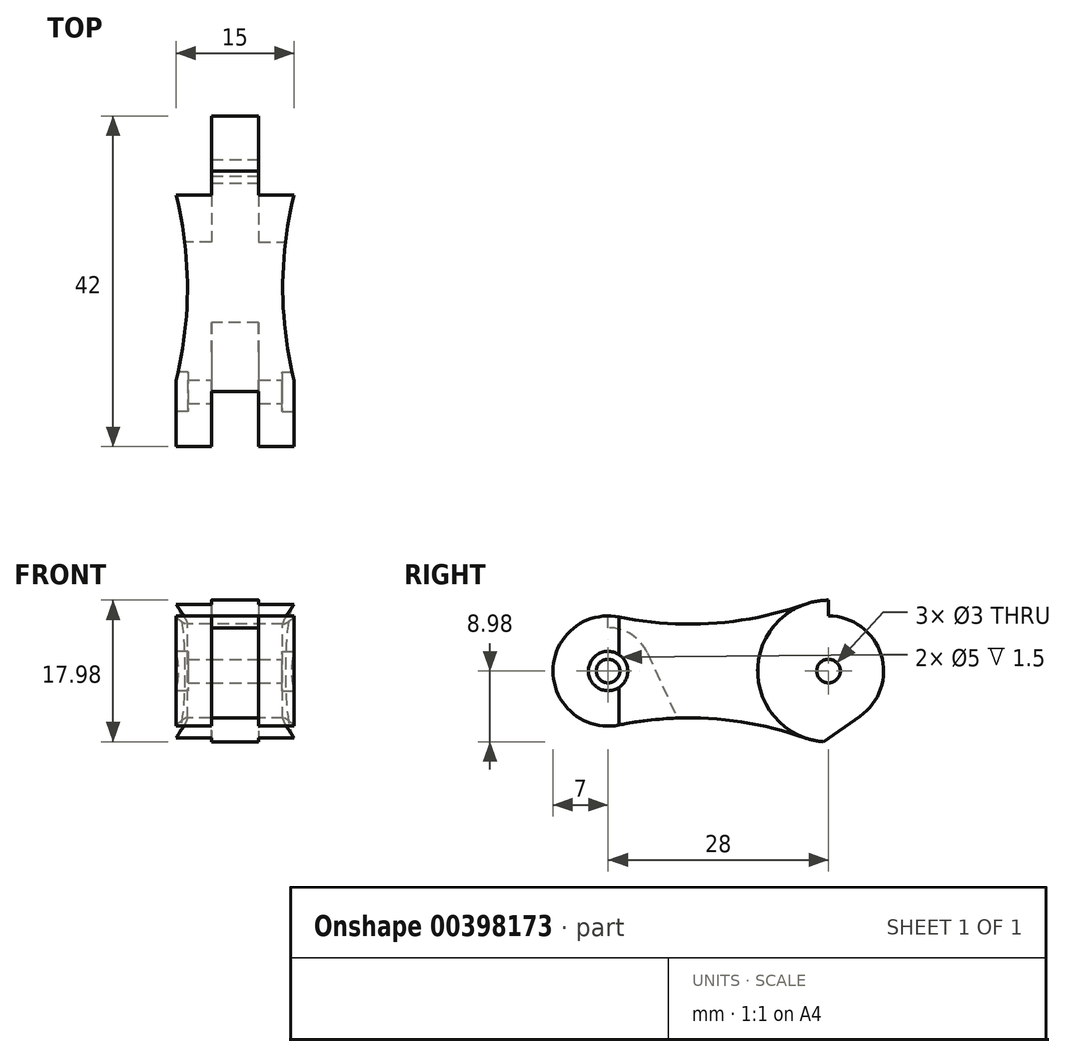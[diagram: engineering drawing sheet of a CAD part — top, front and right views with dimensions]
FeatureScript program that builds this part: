
annotation { "Feature Type Name" : "Feature", "Feature Type Description" : "" }
export const myFeature = defineFeature(function(context is Context, id is Id, definition is map)
    precondition{}
    {
        {
            var Q0;
            Q0=qCreatedBy(makeId("Right.planeOp"),FACE);
            var sketch = newSketch(context, id + "F0", { "sketchPlane" : qUnion([Q0])});
            skArc(sketch, "E0", {"start": v(1.41, 6.86) * mm, "mid": v(-7, 0) * mm, "end": v(1.41, -6.86) * mm});
            skLineSegment(sketch, "E1", {"start": v(-29.92, 0) * mm, "end": v(87.26, 0) * mm, "construction": true});
            skArc(sketch, "E2", {"start": v(25, -8.48) * mm, "mid": v(37, 0) * mm, "end": v(25, 8.48) * mm});
            skArc(sketch, "E3", {"start": v(1.41, 6.86) * mm, "mid": v(13.31, 6.06) * mm, "end": v(25, 8.48) * mm});
            skArc(sketch, "E4", {"start": v(25, -8.48) * mm, "mid": v(13.31, -6.06) * mm, "end": v(1.41, -6.86) * mm});
            skSolve(sketch);
        }
        {
            var Q0;
            Q0=qSketchRegion(id+"F0",true);
            extrude(context, id + "F1", {"entities" : qUnion([Q0]), "depth" : 4.5 * mm});
        }
        {
            var Q0;
            Q0=makeQuery(id+"F1.opExtrude","CAP_FACE",FACE,{"disambiguationData":[OSD([sQuery(id+"F0.wireOp",EDGE,"E0"),sQuery(id+"F0.wireOp",EDGE,"E2"),sQuery(id+"F0.wireOp",EDGE,"E3"),sQuery(id+"F0.wireOp",EDGE,"E4")])],"isStart":false});
            var sketch = newSketch(context, id + "F2", { "sketchPlane" : qUnion([Q0])});
            skArc(sketch, "E5.0", {"start": v(1.41, 6.86) * mm, "mid": v(13.31, 6.06) * mm, "end": v(25, 8.48) * mm});
            skArc(sketch, "E6.0", {"start": v(1.41, 6.86) * mm, "mid": v(0.7, 6.96) * mm, "end": v(0, 7) * mm});
            skArc(sketch, "E7.0", {"start": v(25, -8.48) * mm, "mid": v(37, 0) * mm, "end": v(25, 8.48) * mm});
            skLineSegment(sketch, "E8", {"start": v(0, 5.5) * mm, "end": v(0, 7) * mm});
            skLineSegment(sketch, "E9", {"start": v(0, 0) * mm, "end": v(34.92, 0) * mm, "construction": true});
            skArc(sketch, "E10.0", {"start": v(25, -8.48) * mm, "mid": v(17, -6.47) * mm, "end": v(8.79, -5.98) * mm});
            skArc(sketch, "E11", {"start": v(5, 2.3) * mm, "mid": v(2.97, 4.63) * mm, "end": v(0, 5.5) * mm});
            skLineSegment(sketch, "E12", {"start": v(5, 2.3) * mm, "end": v(8.79, -5.98) * mm});
            skPoint(sketch, "E13.orphan", {"position": v(1.41, -6.86) * mm});
            skSolve(sketch);
        }
        {
            var Q0;
            Q0=qSketchRegion(id+"F2",true);
            extrude(context, id + "F3", {"entities" : qUnion([Q0]), "operationType" : NewBodyOperationType.ADD, "depth" : 6 * mm});
        }
        {
            var Q0;
            Q0=makeQuery(id+"F3.opExtrude","CAP_FACE",FACE,{"disambiguationData":[OSD([sQuery(id+"F2.wireOp",EDGE,"E5.0"),sQuery(id+"F2.wireOp",EDGE,"E6.0"),sQuery(id+"F2.wireOp",EDGE,"a1095cbb-552a-4b33-82fb-9fb0068e6b7f.0"),sQuery(id+"F2.wireOp",EDGE,"E7.0"),sQuery(id+"F2.wireOp",EDGE,"kkhRfJHV-auDH-NZtS-KPEK-8B2iLmtzf0xF"),sQuery(id+"F2.wireOp",EDGE,"E8"),sQuery(id+"F2.wireOp",EDGE,"JRJ70NO1-7vJe-Li3z-EIXT-plhISmGAnEbH")])],"isStart":false});
            var sketch = newSketch(context, id + "F4", { "sketchPlane" : qUnion([Q0])});
            skArc(sketch, "E14.0", {"start": v(0, 7) * mm, "mid": v(-6.96, -0.7) * mm, "end": v(1.41, -6.86) * mm});
            skArc(sketch, "E15.0", {"start": v(1.41, 6.86) * mm, "mid": v(13.31, 6.06) * mm, "end": v(25, 8.48) * mm});
            skArc(sketch, "E16.0", {"start": v(8.79, -5.98) * mm, "mid": v(5.08, -6.26) * mm, "end": v(1.41, -6.86) * mm});
            skArc(sketch, "E17.0", {"start": v(28.44, -8.99) * mm, "mid": v(36.83, 1.74) * mm, "end": v(25, 8.48) * mm});
            skArc(sketch, "E18.0", {"start": v(1.41, 6.86) * mm, "mid": v(0.7, 6.96) * mm, "end": v(0, 7) * mm});
            skArc(sketch, "E19.0", {"start": v(25, -8.48) * mm, "mid": v(17, -6.47) * mm, "end": v(8.79, -5.98) * mm});
            skArc(sketch, "E20.0", {"start": v(25, -8.48) * mm, "mid": v(37, 0) * mm, "end": v(25, 8.48) * mm});
            skSolve(sketch);
        }
        {
            var Q0;
            Q0=qSketchRegion(id+"F4",true);
            extrude(context, id + "F5", {"entities" : qUnion([Q0]), "operationType" : NewBodyOperationType.ADD, "depth" : 4.5 * mm});
        }
        {
            var Q0;
            Q0=makeQuery(id+"F5.opExtrude","CAP_FACE",FACE,{"disambiguationData":[OSD([sQuery(id+"F4.wireOp",EDGE,"E14.0"),sQuery(id+"F4.wireOp",EDGE,"E15.0"),sQuery(id+"F4.wireOp",EDGE,"E16.0"),sQuery(id+"F4.wireOp",EDGE,"98b7fe89-a05e-4f80-a394-89aa36924708.0"),sQuery(id+"F4.wireOp",EDGE,"E17.0"),sQuery(id+"F4.wireOp",EDGE,"E18.0")])],"isStart":false});
            var sketch = newSketch(context, id + "F6", { "sketchPlane" : qUnion([Q0])});
            skCircle(sketch, "E21", {"center": v(28, 0) * mm, "radius": 9 * mm});
            skSolve(sketch);
        }
        {
            var Q0;
            Q0=qSketchRegion(id+"F6",true);
            extrude(context, id + "F7", {"entities" : qUnion([Q0]), "operationType" : NewBodyOperationType.REMOVE, "oppositeDirection" : true, "depth" : 4.5 * mm});
        }
        {
            var Q0;
            Q0=makeQuery(id+"F1.opExtrude","CAP_FACE",FACE,{"disambiguationData":[OSD([sQuery(id+"F0.wireOp",EDGE,"E0"),sQuery(id+"F0.wireOp",EDGE,"E2"),sQuery(id+"F0.wireOp",EDGE,"E3"),sQuery(id+"F0.wireOp",EDGE,"E4")])],"isStart":true});
            var sketch = newSketch(context, id + "F8", { "sketchPlane" : qUnion([Q0])});
            skCircle(sketch, "E22", {"center": v(-28, 0) * mm, "radius": 9 * mm});
            skSolve(sketch);
        }
        {
            var Q0;
            Q0=qSketchRegion(id+"F8",true);
            extrude(context, id + "F9", {"entities" : qUnion([Q0]), "operationType" : NewBodyOperationType.REMOVE, "oppositeDirection" : true, "depth" : 4.5 * mm});
        }
        {
            var Q0;
            Q0=makeQuery(id+"F7.boolean.opBoolean","COPY",FACE,{"derivedFrom":makeQuery(id+"F7.opExtrude","CAP_FACE",FACE,{"disambiguationData":[OSD([sQuery(id+"F6.wireOp",EDGE,"E21")])],"isStart":false})});
            var sketch = newSketch(context, id + "F10", { "sketchPlane" : qUnion([Q0])});
            skArc(sketch, "E23", {"start": v(32, -5.74) * mm, "mid": v(34.68, 2.1) * mm, "end": v(28, 7) * mm});
            skLineSegment(sketch, "E24", {"start": v(28, 9) * mm, "end": v(28, 7) * mm});
            skArc(sketch, "E25", {"start": v(27.36, -8.98) * mm, "mid": v(37, -0.32) * mm, "end": v(28, 9) * mm});
            skLineSegment(sketch, "E26", {"start": v(32, -5.74) * mm, "end": v(27.36, -8.98) * mm});
            skSolve(sketch);
        }
        {
            var Q0;
            Q0=qSketchRegion(id+"F10",true);
            extrude(context, id + "F11", {"entities" : qUnion([Q0]), "operationType" : NewBodyOperationType.REMOVE, "endBound" : BoundingType.THROUGH_ALL, "oppositeDirection" : true, "depth" : 25 * mm});
        }
        {
            var Q0;
            Q0=makeQuery(id+"F5.opExtrude","CAP_FACE",FACE,{"disambiguationData":[OSD([sQuery(id+"F4.wireOp",EDGE,"E14.0"),sQuery(id+"F4.wireOp",EDGE,"E15.0"),sQuery(id+"F4.wireOp",EDGE,"E16.0"),sQuery(id+"F4.wireOp",EDGE,"E17.0"),sQuery(id+"F4.wireOp",EDGE,"E18.0"),sQuery(id+"F4.wireOp",EDGE,"e2e0c06b-e312-4c98-9337-a9e4e4e6bb38.0")])],"isStart":false});
            var sketch = newSketch(context, id + "F12", { "sketchPlane" : qUnion([Q0])});
            skCircle(sketch, "E27", {"center": v(0, 0) * mm, "radius": 1.5 * mm});
            skCircle(sketch, "E28", {"center": v(28, 0) * mm, "radius": 1.5 * mm});
            skSolve(sketch);
        }
        {
            var Q0;
            Q0=qSketchRegion(id+"F12",true);
            extrude(context, id + "F13", {"entities" : qUnion([Q0]), "operationType" : NewBodyOperationType.REMOVE, "endBound" : BoundingType.THROUGH_ALL, "oppositeDirection" : true, "depth" : 25 * mm});
        }
        {
            var Q0;
            Q0=makeQuery(id+"F5.opExtrude","CAP_FACE",FACE,{"disambiguationData":[OSD([sQuery(id+"F4.wireOp",EDGE,"E14.0"),sQuery(id+"F4.wireOp",EDGE,"E15.0"),sQuery(id+"F4.wireOp",EDGE,"E16.0"),sQuery(id+"F4.wireOp",EDGE,"E17.0"),sQuery(id+"F4.wireOp",EDGE,"E18.0"),sQuery(id+"F4.wireOp",EDGE,"e2e0c06b-e312-4c98-9337-a9e4e4e6bb38.0")])],"isStart":false});
            var sketch = newSketch(context, id + "F14", { "sketchPlane" : qUnion([Q0])});
            skCircle(sketch, "E29", {"center": v(0, 0) * mm, "radius": 2.5 * mm});
            skSolve(sketch);
        }
        {
            var Q0;
            Q0=qSketchRegion(id+"F14",true);
            extrude(context, id + "F15", {"entities" : qUnion([Q0]), "operationType" : NewBodyOperationType.REMOVE, "oppositeDirection" : true, "depth" : 1.5 * mm});
        }
        {
            var Q0;
            Q0=makeQuery(id+"F1.opExtrude","CAP_FACE",FACE,{"disambiguationData":[OSD([sQuery(id+"F0.wireOp",EDGE,"E0"),sQuery(id+"F0.wireOp",EDGE,"E2"),sQuery(id+"F0.wireOp",EDGE,"E3"),sQuery(id+"F0.wireOp",EDGE,"E4")])],"isStart":true});
            var sketch = newSketch(context, id + "F16", { "sketchPlane" : qUnion([Q0])});
            skCircle(sketch, "E30", {"center": v(0, 0) * mm, "radius": 2.5 * mm});
            skSolve(sketch);
        }
        {
            var Q0;
            Q0=qSketchRegion(id+"F16",true);
            extrude(context, id + "F17", {"entities" : qUnion([Q0]), "operationType" : NewBodyOperationType.REMOVE, "oppositeDirection" : true, "depth" : 1.5 * mm});
        }
        {
            var Q0;
            Q0=qCreatedBy(makeId("Top.planeOp"),FACE);
            var sketch = newSketch(context, id + "F18", { "sketchPlane" : qUnion([Q0])});
            skCircle(sketch, "E31", {"center": v(-47.5, 13.2) * mm, "radius": 48.94 * mm});
            skCircle(sketch, "E32", {"center": v(62.5, 13.2) * mm, "radius": 48.94 * mm});
            skSolve(sketch);
        }
        {
            var Q0;
            Q0=qSketchRegion(id+"F18",true);
            extrude(context, id + "F19", {"entities" : qUnion([Q0]), "operationType" : NewBodyOperationType.REMOVE, "endBound" : BoundingType.SYMMETRIC, "oppositeDirection" : true, "depth" : 25 * mm});
        }
    });
